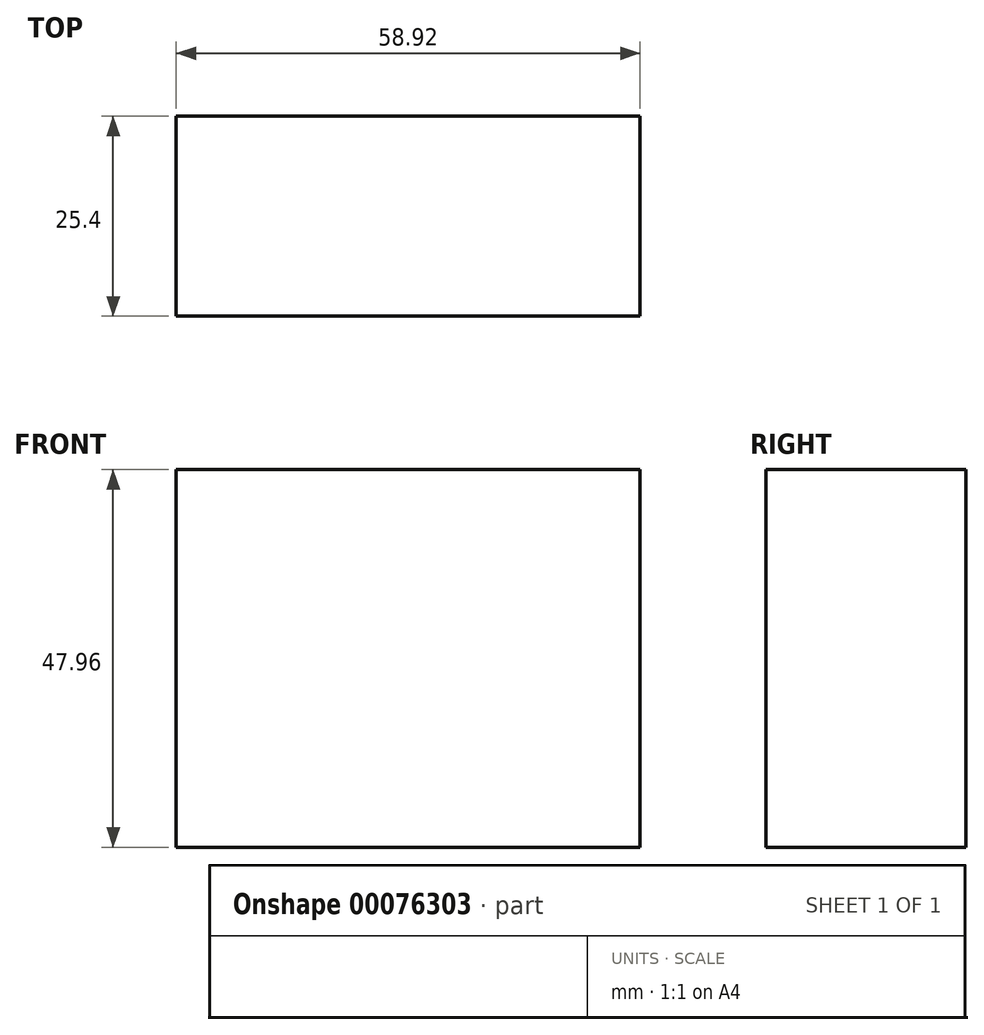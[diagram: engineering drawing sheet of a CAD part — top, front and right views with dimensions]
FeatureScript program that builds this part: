
annotation { "Feature Type Name" : "Feature", "Feature Type Description" : "" }
export const myFeature = defineFeature(function(context is Context, id is Id, definition is map)
    precondition{}
    {
        {
            var Q0;
            Q0=qCreatedBy(makeId("Front.planeOp"),FACE);
            var sketch = newSketch(context, id + "F1", { "sketchPlane" : qUnion([Q0])});
            skLineSegment(sketch, "E0.bottom", {"start": v(29.46, 23.98) * mm, "end": v(-29.46, 23.98) * mm});
            skLineSegment(sketch, "E0.top", {"start": v(29.46, -23.98) * mm, "end": v(-29.46, -23.98) * mm});
            skLineSegment(sketch, "E0.left", {"start": v(29.46, 23.98) * mm, "end": v(29.46, -23.98) * mm});
            skLineSegment(sketch, "E0.right", {"start": v(-29.46, 23.98) * mm, "end": v(-29.46, -23.98) * mm});
            skPoint(sketch, "E0.middle", {"position": v(0, 0) * mm});
            skSolve(sketch);
        }
        {
            var Q0;
            Q0=makeQuery(id+"F1.imprint","IMPRINT",FACE,{"disambiguationData":[TD([[makeQuery(id+"F1.imprint","IMPRINT",EDGE,{"derivedFrom":sQuery(id+"F1.wireOp",EDGE,"E0.bottom")}),1.0]])]});
            extrude(context, id + "F0", {"entities" : qUnion([Q0]), "endBound" : BoundingType.SYMMETRIC, "depth" : 25.4 * mm});
        }
    });
